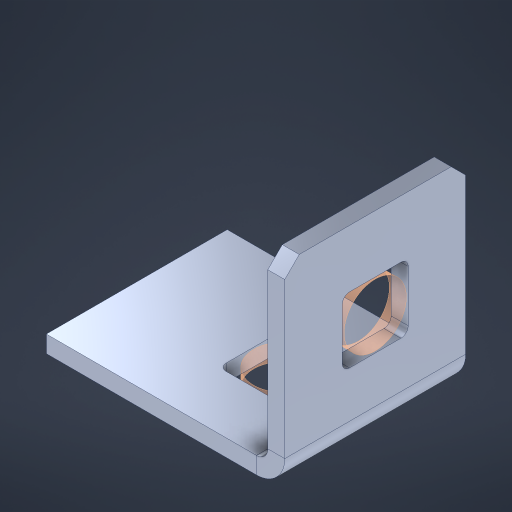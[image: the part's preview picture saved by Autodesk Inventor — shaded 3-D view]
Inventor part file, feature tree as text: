
AUTODESK INVENTOR PART (.ipt)
format: ipt  version: 2023 (Build 270158000, 158)  size: 441,344 bytes
history: native  units: in
note: dims shown in document units (in); Inventor stores cm internally (conversion verified against a paired STEP export)
features: other x75, extrude x69, sheet_metal_op x10, sketch x8, mirror x1, pattern_linear x1, chamfer x1
ambient origin geometry x8: Origin, YZ Plane, XZ Plane, XY Plane, X Axis, Y Axis, Z Axis, Center Point
bodies: Solid1 (feature_tree), Body (feature_tree)
feature tree (165):
  other  "Flange Pattern Plane"
  sheet_metal_op  "Flange Pattern"
  sheet_metal_op  "Body Pattern"
  other  "Arc Length"
  mirror  "Notch Mirror"
  pattern_linear  "Notch Pattern"  Spacing1=0.1875in  [1 undecoded]
  chamfer  "End Chamfer"
  extrude  "Half Cut"  Depth=0.0469in
  sketch  "Sketch1"  dims[d0=2.5in]
  other  "Plate1"
  sketch  "Sketch2"  dims[d1=0.5in]
  other  "Plate2"
  sheet_metal_op  "Bend1"
  sheet_metal_op  "Corner1"
  sketch  "Sketch3"  dims[d2=0.0469in]
  other  "Flange Pattern Sketch"
  sketch  "Sketch7"  dims[d3=0.0469in]
  other  "Srf1"
  other  "Srf2"
  sketch  "Sketch8"  dims[d4=0.0234in]
  sketch  "Sketch9"  dims[d5=0.0938in]
  other  "Srf91"
  sheet_metal_op  "Body Pattern Sketch"
  other  "Srf92"
  sketch  "Sketch13"  dims[d6=0.0469in]
  sketch  "Sketch14"  dims[d7=0.5in d8=90.0deg d9=0.0312in d10=0.1875in d11=0.0469in d12=0.0469in d16=0.182in d17=0.02in d18=0.0469in d19=0.0in d20=0.25in d21=0.25in d46=0.172in d47=1.0in d48=0.0in d49=0.182in d50=0.02in d51=0.25in d52=0.25in d53=0.0469in d54=0.0in d55=0.172in d56=1.0in d57=0.0in d60=0.3937in d62=0.5in d63=0.3937in d65=0.5in d85=0.1227in d86=0.1659in d88=0.04in d89=0.0469in d90=0.0in d91=0.04in d92=0.0491in d95=2.5in d96=0.04in d97=0.25in d98=45.0deg d101=0.0in d102=2.497in d131=0.5in d132=0.3937in d134=0.5in d139=0.5in]
  other  "Srf856"
  other  "Srf1310"
  other  "Srf1311"
  other  "Srf1312"
  other  "Srf1376"
  other  "Srf1377"
  other  "Srf1728"
  other  "Srf1755"
  other  "Srf1878"
  other  "Srf1879"
  other  "Srf1880"
  other  "Srf1881"
  other  "Srf1882"
  other  "Srf1883"
  other  "Srf1884"
  other  "Srf1885"
  other  "Srf1886"
  other  "Srf1887"
  other  "Srf1888"
  other  "Srf1889"
  other  "Srf1890"
  other  "Srf1891"
  other  "Srf1892"
  other  "Srf1893"
  other  "Srf1894"
  other  "Srf1895"
  other  "Srf1896"
  other  "Srf1897"
  other  "Srf1898"
  other  "Srf1899"
  other  "Srf1900"
  other  "Srf1901"
  other  "Srf1902"
  other  "Srf1903"
  other  "Srf1904"
  other  "Srf1905"
  other  "Srf1906"
  other  "Srf1942"
  other  "Srf1943"
  other  "Srf1944"
  other  "Srf1945"
  other  "Srf1946"
  other  "Srf1947"
  other  "Srf1948"
  other  "Srf1949"
  other  "Srf1950"
  other  "Srf1951"
  other  "Srf1952"
  other  "Srf1953"
  other  "Srf1954"
  other  "Srf1955"
  other  "Srf1956"
  other  "Srf1957"
  other  "Srf1958"
  other  "Srf1959"
  other  "Srf1960"
  other  "Srf1961"
  other  "Srf1962"
  other  "Srf1963"
  other  "Srf1964"
  other  "Srf1965"
  other  "Srf1966"
  other  "Srf1967"
  other  "Srf1968"
  other  "Srf1969"
  other  "Srf1970"
  sheet_metal_op  "Flange Stamp"
  sheet_metal_op  "Flange Circle"
  sheet_metal_op  "Body Stamp"
  sheet_metal_op  "Body Circle"
  sheet_metal_op  "Notch"
  extrude  "ExtrusionSrf2"  Depth=0.0469in
  extrude  "ExtrusionSrf92"  Depth=0.182in
  extrude  "ExtrusionSrf856"  Depth=0.02in
  extrude  "ExtrusionSrf1310"  Depth=0.0469in
  extrude  "ExtrusionSrf1311"  TaperAngle=0.0deg  [1 undecoded]
  extrude  "ExtrusionSrf1312"  Depth=0.25in
  extrude  "ExtrusionSrf1376"  Depth=0.25in
  extrude  "ExtrusionSrf1377"  Depth=0.5in
  extrude  "ExtrusionSrf1728"  Depth=0.5in TaperAngle=0.0deg
  extrude  "ExtrusionSrf1755"  Depth=0.182in
  extrude  "ExtrusionSrf1878"  Depth=0.02in
  extrude  "ExtrusionSrf1879"  Depth=0.25in
  extrude  "ExtrusionSrf1880"  Depth=0.25in
  extrude  "ExtrusionSrf1881"  Depth=0.0469in
  extrude  "ExtrusionSrf1882"  TaperAngle=0.0deg  [1 undecoded]
  extrude  "ExtrusionSrf1883"  Depth=0.5in
  extrude  "ExtrusionSrf1884"  Depth=0.5in TaperAngle=0.0deg
  extrude  "ExtrusionSrf1885"  Depth=0.3937in
  extrude  "ExtrusionSrf1886"  Depth=0.5in
  extrude  "ExtrusionSrf1887"  Depth=0.5in
  extrude  "ExtrusionSrf1888"  Depth=0.5in
  extrude  "ExtrusionSrf1889"  Depth=0.5in
  extrude  "ExtrusionSrf1890"  Depth=0.0469in
  extrude  "ExtrusionSrf1891"  TaperAngle=0.0deg  [1 undecoded]
  extrude  "ExtrusionSrf1892"  Depth=0.5in
  extrude  "ExtrusionSrf1893"  Depth=0.5in
  extrude  "ExtrusionSrf1894"  Depth=0.5in
  extrude  "ExtrusionSrf1895"  Depth=0.25in TaperAngle=45.0deg
  extrude  "ExtrusionSrf1896"  TaperAngle=0.0deg  [1 undecoded]
  extrude  "ExtrusionSrf1897"  Depth=0.5in
  extrude  "ExtrusionSrf1898"  Depth=0.5in
  extrude  "ExtrusionSrf1899"  Depth=0.3937in
  extrude  "ExtrusionSrf1900"  Depth=0.5in
  extrude  "ExtrusionSrf1901"  Depth=0.5in
  extrude  "ExtrusionSrf1902"  [1 undecoded]
  extrude  "ExtrusionSrf1903"  [1 undecoded]
  extrude  "ExtrusionSrf1904"  [1 undecoded]
  extrude  "ExtrusionSrf1905"  [1 undecoded]
  extrude  "ExtrusionSrf1906"  [1 undecoded]
  extrude  "ExtrusionSrf1942"  [1 undecoded]
  extrude  "ExtrusionSrf1943"  [1 undecoded]
  extrude  "ExtrusionSrf1944"  [1 undecoded]
  extrude  "ExtrusionSrf1945"  [1 undecoded]
  extrude  "ExtrusionSrf1946"  [1 undecoded]
  extrude  "ExtrusionSrf1947"  [1 undecoded]
  extrude  "ExtrusionSrf1948"  [1 undecoded]
  extrude  "ExtrusionSrf1949"  [1 undecoded]
  extrude  "ExtrusionSrf1950"  [1 undecoded]
  extrude  "ExtrusionSrf1951"  [1 undecoded]
  extrude  "ExtrusionSrf1952"  [1 undecoded]
  extrude  "ExtrusionSrf1953"  [1 undecoded]
  extrude  "ExtrusionSrf1954"  [1 undecoded]
  extrude  "ExtrusionSrf1955"  [1 undecoded]
  extrude  "ExtrusionSrf1956"  [1 undecoded]
  extrude  "ExtrusionSrf1957"  [1 undecoded]
  extrude  "ExtrusionSrf1958"  [1 undecoded]
  extrude  "ExtrusionSrf1959"  [1 undecoded]
  extrude  "ExtrusionSrf1960"  [1 undecoded]
  extrude  "ExtrusionSrf1961"  [1 undecoded]
  extrude  "ExtrusionSrf1962"  [1 undecoded]
  extrude  "ExtrusionSrf1963"  [1 undecoded]
  extrude  "ExtrusionSrf1964"  [1 undecoded]
  extrude  "ExtrusionSrf1965"  [1 undecoded]
  extrude  "ExtrusionSrf1966"  [1 undecoded]
  extrude  "ExtrusionSrf1967"  [1 undecoded]
  extrude  "ExtrusionSrf1968"  [1 undecoded]
  extrude  "ExtrusionSrf1969"  [1 undecoded]
  extrude  "ExtrusionSrf1970"  [1 undecoded]
note: 39 required parameter values undecoded (feature->parameter linkage not recoverable at this tier; creation-order binding heuristic only, values carry confidence <= 0.55)
